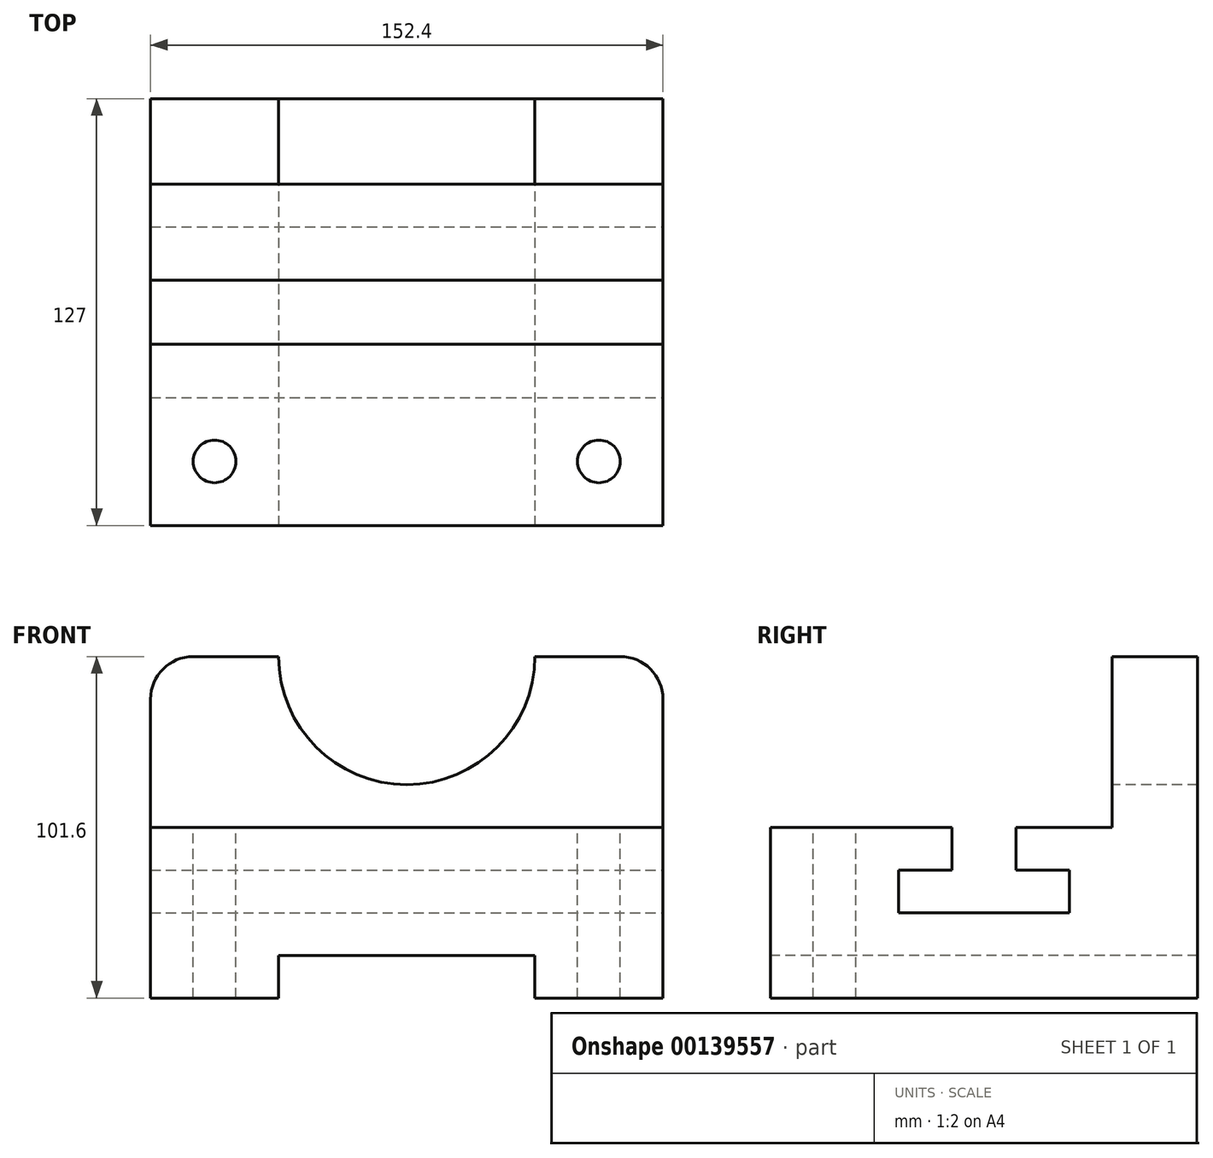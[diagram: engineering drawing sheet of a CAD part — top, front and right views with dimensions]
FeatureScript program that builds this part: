
annotation { "Feature Type Name" : "Feature", "Feature Type Description" : "" }
export const myFeature = defineFeature(function(context is Context, id is Id, definition is map)
    precondition{}
    {
        {
            var Q0;
            Q0=qCreatedBy(makeId("Right.planeOp"),FACE);
            var sketch = newSketch(context, id + "F0", { "sketchPlane" : qUnion([Q0])});
            skLineSegment(sketch, "E0", {"start": v(-111, 0) * mm, "end": v(16, 0) * mm});
            skLineSegment(sketch, "E1", {"start": v(-111, 0) * mm, "end": v(-111, 50.8) * mm});
            skLineSegment(sketch, "E2", {"start": v(-111, 50.8) * mm, "end": v(16, 50.8) * mm});
            skLineSegment(sketch, "E3", {"start": v(16, 50.8) * mm, "end": v(16, 0) * mm});
            skLineSegment(sketch, "E4", {"start": v(-9.4, 50.8) * mm, "end": v(-9.4, 101.6) * mm});
            skLineSegment(sketch, "E5", {"start": v(-9.4, 101.6) * mm, "end": v(-9.4, 101.6) * mm});
            skLineSegment(sketch, "E6", {"start": v(16, 50.8) * mm, "end": v(16, 101.6) * mm});
            skLineSegment(sketch, "E7", {"start": v(16, 101.6) * mm, "end": v(-9.4, 101.6) * mm});
            skSolve(sketch);
        }
        {
            var Q0;
            Q0 = qSketchRegion(id + "F0", true);
            extrude(context, id + "F1", {"entities" : qUnion([Q0]), "depth" : 152.4 * mm});
        }
        {
            var Q0;
            Q0=makeQuery(id+"F1.opExtrude","CAP_EDGE",EDGE,{"disambiguationData":[OSD([sQuery(id+"F0.wireOp",EDGE,"E7")])],"isStart":false});
            var Q1;
            Q1=makeQuery(id+"F1.opExtrude","CAP_EDGE",EDGE,{"disambiguationData":[OSD([sQuery(id+"F0.wireOp",EDGE,"E7")])],"isStart":true});
            fillet(context, id + "F2", {"entities" : qUnion([Q0, Q1]), "radius" : 12.7 * mm, "tangentPropagation" : true, "allowEdgeOverflow" : false});
        }
        {
            var Q0;
            Q0=makeQuery(id+"F1.opExtrude","CAP_FACE",FACE,{"disambiguationData":[OSD([sQuery(id+"F0.wireOp",EDGE,"E0"),sQuery(id+"F0.wireOp",EDGE,"E1"),sQuery(id+"F0.wireOp",EDGE,"E2"),sQuery(id+"F0.wireOp",EDGE,"E3"),sQuery(id+"F0.wireOp",EDGE,"E4"),sQuery(id+"F0.wireOp",EDGE,"E6"),sQuery(id+"F0.wireOp",EDGE,"E7")])],"isStart":false});
            var sketch = newSketch(context, id + "F3", { "sketchPlane" : qUnion([Q0])});
            skLineSegment(sketch, "E8", {"start": v(-57.03, 50.8) * mm, "end": v(-57.03, 38.1) * mm});
            skLineSegment(sketch, "E9", {"start": v(-57.03, 38.1) * mm, "end": v(-72.9, 38.1) * mm});
            skLineSegment(sketch, "E10", {"start": v(-72.9, 38.1) * mm, "end": v(-72.9, 25.4) * mm});
            skLineSegment(sketch, "E11", {"start": v(-72.9, 25.4) * mm, "end": v(-22.1, 25.4) * mm});
            skLineSegment(sketch, "E12", {"start": v(-22.1, 25.4) * mm, "end": v(-22.1, 38.1) * mm});
            skLineSegment(sketch, "E13", {"start": v(-22.1, 38.1) * mm, "end": v(-37.98, 38.1) * mm});
            skLineSegment(sketch, "E14", {"start": v(-37.98, 38.1) * mm, "end": v(-37.98, 50.8) * mm});
            skLineSegment(sketch, "E15", {"start": v(-57.03, 50.8) * mm, "end": v(-37.98, 50.8) * mm});
            skSolve(sketch);
        }
        {
            var Q0;
            Q0 = qSketchRegion(id + "F3", true);
            extrude(context, id + "F4", {"entities" : qUnion([Q0]), "operationType" : NewBodyOperationType.REMOVE, "endBound" : BoundingType.THROUGH_ALL, "oppositeDirection" : true, "depth" : 25.4 * mm});
        }
        {
            var Q0;
            Q0=makeQuery(id+"F1.opExtrude","SWEPT_FACE",FACE,{"disambiguationData":[OSD([sQuery(id+"F0.wireOp",EDGE,"E1")])]});
            var sketch = newSketch(context, id + "F5", { "sketchPlane" : qUnion([Q0])});
            skLineSegment(sketch, "E16", {"start": v(38.1, 0) * mm, "end": v(38.1, 12.7) * mm});
            skLineSegment(sketch, "E17", {"start": v(38.1, 12.7) * mm, "end": v(114.3, 12.7) * mm});
            skLineSegment(sketch, "E18", {"start": v(114.3, 12.7) * mm, "end": v(114.3, 0) * mm});
            skLineSegment(sketch, "E19", {"start": v(38.1, 0) * mm, "end": v(114.3, 0) * mm});
            skSolve(sketch);
        }
        {
            var Q0;
            Q0 = qSketchRegion(id + "F5", true);
            extrude(context, id + "F6", {"entities" : qUnion([Q0]), "operationType" : NewBodyOperationType.REMOVE, "endBound" : BoundingType.THROUGH_ALL, "oppositeDirection" : true, "depth" : 25.4 * mm});
        }
        {
            var Q0;
            {var subQ4=sQuery(id+"F0.wireOp",EDGE,"E2");var subQ5=sQuery(id+"F0.wireOp",EDGE,"E1");Q0=makeQuery(id+"F4.boolean.opBoolean","SPLIT",FACE,{"disambiguationData":[TD([makeQuery(id+"F1.opExtrude","SWEPT_FACE",FACE,{"disambiguationData":[OSD([subQ5])]})])],"derivedFrom":makeQuery(id+"F1.opExtrude","SWEPT_FACE",FACE,{"disambiguationData":[OSD([subQ4])]})});}
            var sketch = newSketch(context, id + "F7", { "sketchPlane" : qUnion([Q0])});
            skCircle(sketch, "E20", {"center": v(19.05, -91.95) * mm, "radius": 6.35 * mm});
            skLineSegment(sketch, "E21", {"start": v(76.2, -111) * mm, "end": v(76.2, -37.97) * mm});
            skCircle(sketch, "E22.MirrorC", {"center": v(133.35, -91.95) * mm, "radius": 6.35 * mm});
            skSolve(sketch);
        }
        {
            var Q0;
            Q0 = qSketchRegion(id + "F7", true);
            extrude(context, id + "F8", {"entities" : qUnion([Q0]), "operationType" : NewBodyOperationType.REMOVE, "endBound" : BoundingType.THROUGH_ALL, "oppositeDirection" : true, "depth" : 25.4 * mm});
        }
        {
            var Q0;
            Q0=makeQuery(id+"F1.opExtrude","SWEPT_FACE",FACE,{"disambiguationData":[OSD([sQuery(id+"F0.wireOp",EDGE,"E4")])]});
            var sketch = newSketch(context, id + "F9", { "sketchPlane" : qUnion([Q0])});
            skCircle(sketch, "E23", {"center": v(76.2, 101.6) * mm, "radius": 38.1 * mm});
            skSolve(sketch);
        }
        {
            var Q0;
            Q0 = qSketchRegion(id + "F9", true);
            extrude(context, id + "F10", {"entities" : qUnion([Q0]), "operationType" : NewBodyOperationType.REMOVE, "endBound" : BoundingType.THROUGH_ALL, "oppositeDirection" : true, "depth" : 25.4 * mm});
        }
    });
